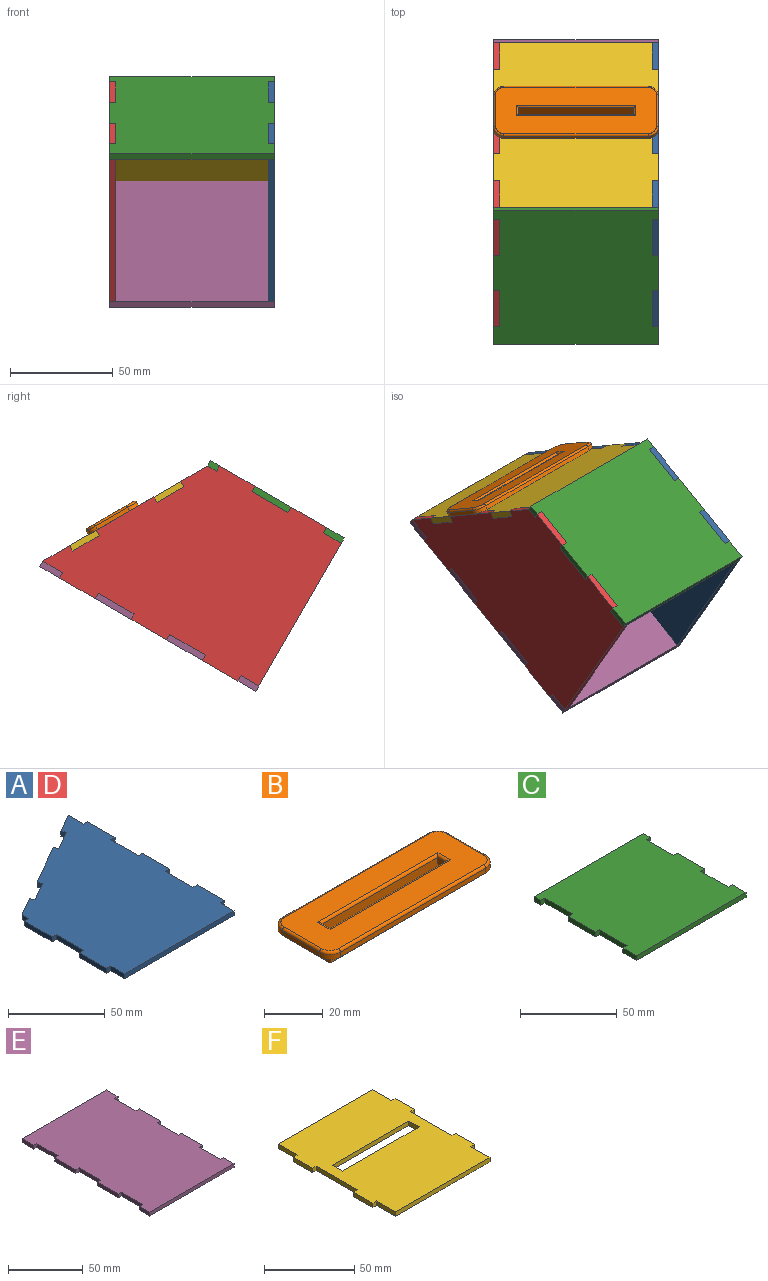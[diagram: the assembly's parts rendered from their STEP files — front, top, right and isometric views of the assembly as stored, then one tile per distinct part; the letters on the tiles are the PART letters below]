
ASSEMBLY  parts=6 mates=15
PART A: 34 faces, bbox 86x121.2x3 mm
  f0: plane 20x3mm, normal (1,0,0), area 60mm2, adj f1,f31,f32,f33
  f1: plane 3x3mm, normal (0,-1,0), area 9mm2, adj f0,f2,f32,f33
  f2: plane 20x3mm, normal (1,0,0), area 60mm2, adj f1,f3,f32,f33
  f3: plane 3x3mm, normal (0,1,0), area 9mm2, adj f2,f4,f32,f33
  f4: plane 20x3mm, normal (1,0,0), area 60mm2, adj f3,f5,f32,f33
  f5: plane 3x3mm, normal (0,-1,0), area 9mm2, adj f4,f6,f32,f33
  f6: plane 20x3mm, normal (1,0,0), area 60mm2, adj f5,f7,f32,f33
  f7: plane 3x3mm, normal (0,1,0), area 9mm2, adj f6,f8,f32,f33
  f8: plane 11.19x3mm, normal (1,0,0), area 33.6mm2, adj f7,f9,f32,f33
  f9: plane 12.99x7.5mm, normal (-0.5,0.87,0), area 45mm2, adj f8,f10,f32,f33
  f10: plane 3x2.6mm, normal (-0.87,-0.5,0), area 9mm2, adj f9,f11,f32,f33
  f11: plane 12.99x7.5mm, normal (-0.5,0.87,0), area 45mm2, adj f10,f12,f32,f33
  f12: plane 3x2.6mm, normal (0.87,0.5,0), area 9mm2, adj f11,f13,f32,f33
  f13: plane 28.04x16.19mm, normal (-0.5,0.87,0), area 97.1mm2, adj f12,f14,f32,f33
  f14: plane 3x2.6mm, normal (-0.87,-0.5,0), area 9mm2, adj f13,f15,f32,f33
  f15: plane 12.99x7.5mm, normal (-0.5,0.87,0), area 45mm2, adj f14,f16,f32,f33
  f16: plane 3x2.6mm, normal (0.87,0.5,0), area 9mm2, adj f15,f17,f32,f33
  f17: plane 12.99x7.5mm, normal (-0.5,0.87,0), area 45mm2, adj f16,f18,f32,f33
  f18: plane 5x3mm, normal (-1,0,0), area 15mm2, adj f17,f19,f32,f33
  f19: plane 3x3mm, normal (0,1,0), area 9mm2, adj f18,f20,f32,f33
  f20: plane 20x3mm, normal (-1,0,0), area 60mm2, adj f19,f21,f32,f33
  f21: plane 3x3mm, normal (0,-1,0), area 9mm2, adj f20,f22,f32,f33
  f22: plane 20x3mm, normal (-1,0,0), area 60mm2, adj f21,f23,f32,f33
  f23: plane 3x3mm, normal (0,1,0), area 9mm2, adj f22,f24,f32,f33
  f24: plane 20x3mm, normal (-1,0,0), area 60mm2, adj f23,f25,f32,f33
  f25: plane 3x3mm, normal (0,-1,0), area 9mm2, adj f24,f26,f32,f33
  f26: plane 10x3mm, normal (-1,0,0), area 30mm2, adj f25,f27,f32,f33
  f27: plane 80x3mm, normal (0,-1,0), area 240mm2, adj f26,f28,f32,f33
  f28: plane 10x3mm, normal (1,0,0), area 30mm2, adj f27,f29,f32,f33
  f29: plane 3x3mm, normal (0,-1,0), area 9mm2, adj f28,f30,f32,f33
  f30: plane 20x3mm, normal (1,0,0), area 60mm2, adj f29,f31,f32,f33
  f31: plane 3x3mm, normal (0,1,0), area 9mm2, adj f0,f30,f32,f33
  f32: plane 121.19x86mm, normal (0,0,1), area 8057.5mm2, adj f0,f1,f2,f3,f4,f5,f6,f7
  f33: plane 121.19x86mm, normal (0,0,-1), area 8057.5mm2, adj f0,f1,f2,f3,f4,f5,f6,f7
PART B: 31 faces, bbox 80.8x28.8x13 mm
  f0: plane 80x28mm, normal (0,0,-1), area 1738.5mm2, adj f1,f2,f3,f8,f10,f11,f12,f13
  f1: plane 70x2mm, normal (0,-1,0), area 140mm2, adj f0,f15,f18,f24
  f2: plane 18x2mm, normal (1,0,0), area 36mm2, adj f0,f15,f16,f25
  f3: plane 70x2mm, normal (0,1,0), area 140mm2, adj f0,f16,f17,f21
  f4: plane 12x4mm, normal (1,0,0), area 48mm2, adj f5,f7,f14,f29
  f5: plane 56x12mm, normal (0,-1,0), area 672mm2, adj f4,f6,f14,f27
  f6: plane 12x4mm, normal (-1,0,0), area 48mm2, adj f5,f7,f14,f28
  f7: plane 56x12mm, normal (0,1,0), area 672mm2, adj f4,f6,f14,f30
  f8: plane 18x2mm, normal (-1,0,0), area 36mm2, adj f0,f17,f18,f20
  f9: plane 78x26mm, normal (0,0,1), area 1666.3mm2, adj f19,f20,f21,f22,f23,f24,f25,f26
  f10: plane 60x10mm, normal (0,-1,0), area 600mm2, adj f0,f11,f13,f14
  f11: plane 10x8mm, normal (1,0,0), area 80mm2, adj f0,f10,f12,f14
  f12: plane 60x10mm, normal (0,1,0), area 600mm2, adj f0,f11,f13,f14
  f13: plane 10x8mm, normal (-1,0,0), area 80mm2, adj f0,f10,f12,f14
  f14: plane 60x8mm, normal (0,0,-1), area 256mm2, adj f4,f5,f6,f7,f10,f11,f12,f13
  f15: cylinder r=5mm len=5mm, axis (0,0,-1), area 15.7mm2, adj f0,f1,f2,f26
  f16: cylinder r=5mm len=5mm, axis (0,0,1), area 15.7mm2, adj f0,f2,f3,f23
  f17: cylinder r=5mm len=5mm, axis (0,0,-1), area 15.7mm2, adj f0,f3,f8,f19
  f18: cylinder r=5mm len=5mm, axis (0,0,1), area 15.7mm2, adj f0,f1,f8,f22
  f19: torus R=4mm, axis (0,0,1), area 11.4mm2, adj f9,f17,f20,f21
  f20: cylinder r=1mm len=18mm, axis (0,1,0), area 28.3mm2, adj f8,f9,f19,f22
  f21: cylinder r=1mm len=70mm, axis (1,0,0), area 110mm2, adj f3,f9,f19,f23
  f22: torus R=4mm, axis (0,0,1), area 11.4mm2, adj f9,f18,f20,f24
  f23: torus R=4mm, axis (0,0,1), area 11.4mm2, adj f9,f16,f21,f25
  f24: cylinder r=1mm len=70mm, axis (-1,0,0), area 110mm2, adj f1,f9,f22,f26
  f25: cylinder r=1mm len=18mm, axis (0,-1,0), area 28.3mm2, adj f2,f9,f23,f26
  f26: torus R=4mm, axis (0,0,1), area 11.4mm2, adj f9,f15,f24,f25
  f27: cylinder r=1mm len=58mm, axis (-1,0,0), area 89.1mm2, adj f5,f9,f28,f29
  f28: cylinder r=1mm len=6mm, axis (0,1,0), area 7.4mm2, adj f6,f9,f27,f30
  f29: cylinder r=1mm len=6mm, axis (0,-1,0), area 7.4mm2, adj f4,f9,f27,f30
  f30: cylinder r=1mm len=58mm, axis (1,0,0), area 89.1mm2, adj f7,f9,f28,f29
PART C: 22 faces, bbox 80x75x3 mm
  f0: plane 10x3mm, normal (-1,0,0), area 30mm2, adj f1,f19,f20,f21
  f1: plane 80x3mm, normal (0,-1,0), area 240mm2, adj f0,f2,f20,f21
  f2: plane 10x3mm, normal (1,0,0), area 30mm2, adj f1,f3,f20,f21
  f3: plane 3x3mm, normal (0,1,0), area 9mm2, adj f2,f4,f20,f21
  f4: plane 20x3mm, normal (1,0,0), area 60mm2, adj f3,f5,f20,f21
  f5: plane 3x3mm, normal (0,-1,0), area 9mm2, adj f4,f6,f20,f21
  f6: plane 20x3mm, normal (1,0,0), area 60mm2, adj f5,f7,f20,f21
  f7: plane 3x3mm, normal (0,1,0), area 9mm2, adj f6,f8,f20,f21
  f8: plane 20x3mm, normal (1,0,0), area 60mm2, adj f7,f9,f20,f21
  f9: plane 3x3mm, normal (0,-1,0), area 9mm2, adj f8,f10,f20,f21
  f10: plane 5x3mm, normal (1,0,0), area 15mm2, adj f9,f11,f20,f21
  f11: plane 80x3mm, normal (0,1,0), area 240mm2, adj f10,f12,f20,f21
  f12: plane 5x3mm, normal (-1,0,0), area 15mm2, adj f11,f13,f20,f21
  f13: plane 3x3mm, normal (0,-1,0), area 9mm2, adj f12,f14,f20,f21
  f14: plane 20x3mm, normal (-1,0,0), area 60mm2, adj f13,f15,f20,f21
  f15: plane 3x3mm, normal (0,1,0), area 9mm2, adj f14,f16,f20,f21
  f16: plane 20x3mm, normal (-1,0,0), area 60mm2, adj f15,f17,f20,f21
  f17: plane 3x3mm, normal (0,-1,0), area 9mm2, adj f16,f18,f20,f21
  f18: plane 20x3mm, normal (-1,0,0), area 60mm2, adj f17,f19,f20,f21
  f19: plane 3x3mm, normal (0,1,0), area 9mm2, adj f0,f18,f20,f21
  f20: plane 80x75mm, normal (0,0,1), area 5760mm2, adj f0,f1,f2,f3,f4,f5,f6,f7
  f21: plane 80x75mm, normal (0,0,-1), area 5760mm2, adj f0,f1,f2,f3,f4,f5,f6,f7
PART D: same geometry as A
PART E: 30 faces, bbox 80x121.2x3 mm
  f0: plane 20x3mm, normal (-1,0,0), area 60mm2, adj f1,f27,f28,f29
  f1: plane 3x3mm, normal (0,1,0), area 9mm2, adj f0,f2,f28,f29
  f2: plane 10x3mm, normal (-1,0,0), area 30mm2, adj f1,f3,f28,f29
  f3: plane 80x3mm, normal (0,-1,0), area 240mm2, adj f2,f4,f28,f29
  f4: plane 10x3mm, normal (1,0,0), area 30mm2, adj f3,f5,f28,f29
  f5: plane 3x3mm, normal (0,1,0), area 9mm2, adj f4,f6,f28,f29
  f6: plane 20x3mm, normal (1,0,0), area 60mm2, adj f5,f7,f28,f29
  f7: plane 3x3mm, normal (0,-1,0), area 9mm2, adj f6,f8,f28,f29
  f8: plane 20x3mm, normal (1,0,0), area 60mm2, adj f7,f9,f28,f29
  f9: plane 3x3mm, normal (0,1,0), area 9mm2, adj f8,f10,f28,f29
  f10: plane 20x3mm, normal (1,0,0), area 60mm2, adj f9,f11,f28,f29
  f11: plane 3x3mm, normal (0,-1,0), area 9mm2, adj f10,f12,f28,f29
  f12: plane 20x3mm, normal (1,0,0), area 60mm2, adj f11,f13,f28,f29
  f13: plane 3x3mm, normal (0,1,0), area 9mm2, adj f12,f14,f28,f29
  f14: plane 20x3mm, normal (1,0,0), area 60mm2, adj f13,f15,f28,f29
  f15: plane 3x3mm, normal (0,-1,0), area 9mm2, adj f14,f16,f28,f29
  f16: plane 11.19x3mm, normal (1,0,0), area 33.6mm2, adj f15,f17,f28,f29
  f17: plane 80x3mm, normal (0,1,0), area 240mm2, adj f16,f18,f28,f29
  f18: plane 11.19x3mm, normal (-1,0,0), area 33.6mm2, adj f17,f19,f28,f29
  f19: plane 3x3mm, normal (0,-1,0), area 9mm2, adj f18,f20,f28,f29
  f20: plane 20x3mm, normal (-1,0,0), area 60mm2, adj f19,f21,f28,f29
  f21: plane 3x3mm, normal (0,1,0), area 9mm2, adj f20,f22,f28,f29
  f22: plane 20x3mm, normal (-1,0,0), area 60mm2, adj f21,f23,f28,f29
  f23: plane 3x3mm, normal (0,-1,0), area 9mm2, adj f22,f24,f28,f29
  f24: plane 20x3mm, normal (-1,0,0), area 60mm2, adj f23,f25,f28,f29
  f25: plane 3x3mm, normal (0,1,0), area 9mm2, adj f24,f26,f28,f29
  f26: plane 20x3mm, normal (-1,0,0), area 60mm2, adj f25,f27,f28,f29
  f27: plane 3x3mm, normal (0,-1,0), area 9mm2, adj f0,f26,f28,f29
  f28: plane 121.19x80mm, normal (0,0,1), area 9335mm2, adj f0,f1,f2,f3,f4,f5,f6,f7
  f29: plane 121.19x80mm, normal (0,0,-1), area 9335mm2, adj f0,f1,f2,f3,f4,f5,f6,f7
PART F: 26 faces, bbox 80x92.4x3 mm
  f0: plane 15x3mm, normal (-1,0,0), area 45mm2, adj f1,f23,f24,f25
  f1: plane 74x3mm, normal (0,-1,0), area 222mm2, adj f0,f2,f24,f25
  f2: plane 15x3mm, normal (1,0,0), area 45mm2, adj f1,f3,f24,f25
  f3: plane 3x3mm, normal (0,-1,0), area 9mm2, adj f2,f4,f24,f25
  f4: plane 15x3mm, normal (1,0,0), area 45mm2, adj f3,f5,f24,f25
  f5: plane 3x3mm, normal (0,1,0), area 9mm2, adj f4,f6,f24,f25
  f6: plane 32.38x3mm, normal (1,0,0), area 97.1mm2, adj f5,f7,f24,f25
  f7: plane 3x3mm, normal (0,-1,0), area 9mm2, adj f6,f8,f24,f25
  f8: plane 15x3mm, normal (1,0,0), area 45mm2, adj f7,f9,f24,f25
  f9: plane 3x3mm, normal (0,1,0), area 9mm2, adj f8,f10,f24,f25
  f10: plane 15x3mm, normal (1,0,0), area 45mm2, adj f9,f11,f24,f25
  f11: plane 74x3mm, normal (0,1,0), area 222mm2, adj f10,f12,f24,f25
  f12: plane 15x3mm, normal (-1,0,0), area 45mm2, adj f11,f13,f24,f25
  f13: plane 3x3mm, normal (0,1,0), area 9mm2, adj f12,f14,f24,f25
  f14: plane 15x3mm, normal (-1,0,0), area 45mm2, adj f13,f15,f24,f25
  f15: plane 3x3mm, normal (0,-1,0), area 9mm2, adj f14,f16,f24,f25
  f16: plane 32.38x3mm, normal (-1,0,0), area 97.1mm2, adj f15,f17,f24,f25
  f17: plane 3x3mm, normal (0,1,0), area 9mm2, adj f16,f18,f24,f25
  f18: plane 15x3mm, normal (-1,0,0), area 45mm2, adj f17,f23,f24,f25
  f19: plane 60x3mm, normal (0,1,0), area 180mm2, adj f20,f22,f24,f25
  f20: plane 8x3mm, normal (1,0,0), area 24mm2, adj f19,f21,f24,f25
  f21: plane 60x3mm, normal (0,-1,0), area 180mm2, adj f20,f22,f24,f25
  f22: plane 8x3mm, normal (-1,0,0), area 24mm2, adj f19,f21,f24,f25
  f23: plane 3x3mm, normal (0,-1,0), area 9mm2, adj f0,f18,f24,f25
  f24: plane 92.38x80mm, normal (0,0,1), area 6535.8mm2, adj f0,f1,f2,f3,f4,f5,f6,f7
  f25: plane 92.38x80mm, normal (0,0,-1), area 6535.8mm2, adj f0,f1,f2,f3,f4,f5,f6,f7
PLACE A rot(axis=(0.25,0.94,0.25),93.8deg) t=(35.94,164.2,-126.55)mm
PLACE B rot(axis=(-1,0,0),30deg) t=(-1.06,202.56,10.22)mm
PLACE C rot(axis=(1,0,0),30deg) t=(105.2,168.15,43.01)mm
PLACE D rot(axis=(0.25,0.94,0.25),93.8deg) t=(-41.06,164.2,-126.55)mm
PLACE E rot(axis=(1,0,0),30deg) t=(14.45,134.73,-72.13)mm
PLACE F rot(axis=(-1,0,0),30deg) t=(-13.81,251.77,-21.66)mm
MATE planar A.f32 <-> C.f10  axis (1,0,0) through (38.94,152.63,34.04)mm
MATE planar B.f12 <-> F.f21  axis (0,0.87,-0.5) through (-1.06,203.52,3.89)mm
MATE planar D.f2 <-> E.f29  axis (0,0.5,-0.87) through (-39.56,185.47,-42.84)mm
MATE planar C.f21 <-> D.f26  axis (0,0.5,-0.87) through (-1.06,124.39,17.74)mm
MATE planar A.f6 <-> E.f29  axis (0,0.5,-0.87) through (37.44,220.11,-22.84)mm
MATE planar F.f25 <-> A.f11  axis (0,-0.5,-0.87) through (-1.06,197.59,9.62)mm
MATE planar F.f3 <-> A.f16  axis (0,-0.87,0.5) through (37.44,169.2,27.75)mm
MATE planar A.f19 <-> C.f9  axis (0,0.87,0.5) through (37.44,151.88,35.34)mm
MATE planar E.f14 <-> A.f33  axis (1,0,0) through (35.94,218.61,-20.24)mm
MATE planar E.f1 <-> D.f29  axis (0,0.87,0.5) through (-39.56,141.42,-66.54)mm
MATE planar E.f5 <-> A.f29  axis (0,0.87,0.5) through (37.44,141.42,-66.54)mm
MATE planar A.f32 <-> F.f8  axis (1,0,0) through (38.94,156.56,-13.75)mm
MATE planar B.f16 <-> F.f24  axis (0,-0.5,-0.87) through (33.94,210.35,5.72)mm
MATE planar B.f5 <-> B.f13  axis (0,-0.87,0.5) through (-29.06,202.29,5.76)mm
MATE planar D.f32 <-> E.f20  axis (1,0,0) through (-38.06,156.56,-13.75)mm
